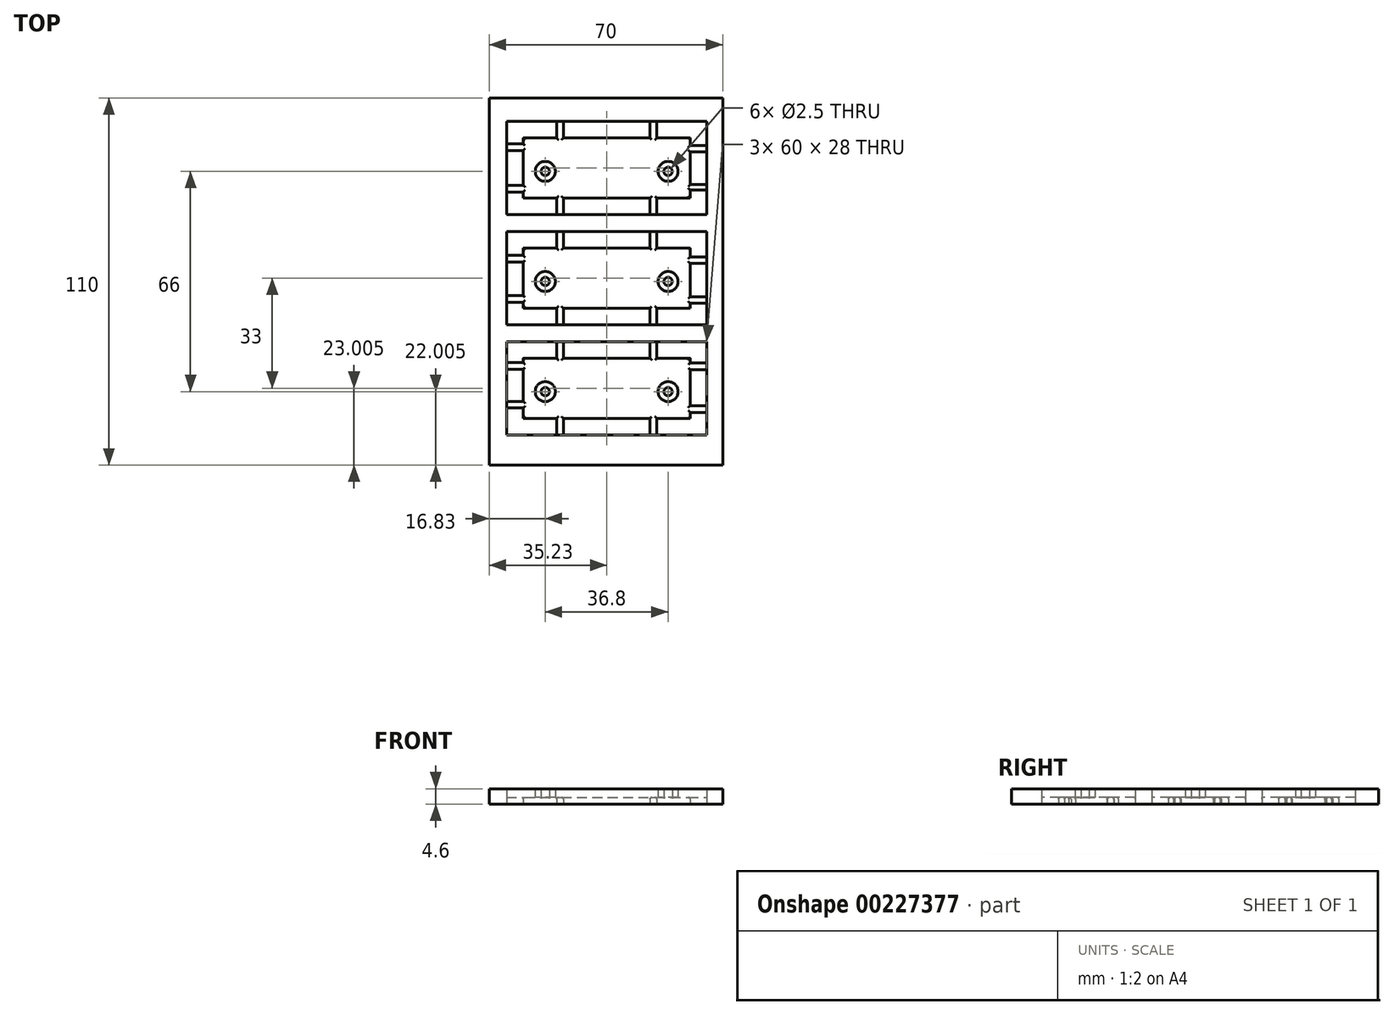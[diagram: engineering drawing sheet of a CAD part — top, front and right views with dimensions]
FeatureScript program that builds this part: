
annotation { "Feature Type Name" : "Feature", "Feature Type Description" : "" }
export const myFeature = defineFeature(function(context is Context, id is Id, definition is map)
    precondition{}
    {
        {
            var Q0;
            Q0=qCreatedBy(makeId("Top.planeOp"),FACE);
            var sketch = newSketch(context, id + "F0", { "sketchPlane" : qUnion([Q0])});
            skLineSegment(sketch, "E0.bottom", {"start": v(-14.26, 31.33) * mm, "end": v(35.74, 31.33) * mm});
            skLineSegment(sketch, "E0.top", {"start": v(-14.26, 13.33) * mm, "end": v(35.74, 13.33) * mm});
            skLineSegment(sketch, "E0.left", {"start": v(-14.26, 31.33) * mm, "end": v(-14.26, 13.33) * mm});
            skLineSegment(sketch, "E0.right", {"start": v(35.74, 31.33) * mm, "end": v(35.74, 13.33) * mm});
            skLineSegment(sketch, "E1.bottom", {"start": v(-14.26, -1.67) * mm, "end": v(35.74, -1.67) * mm});
            skLineSegment(sketch, "E1.top", {"start": v(-14.26, -19.67) * mm, "end": v(35.74, -19.67) * mm});
            skLineSegment(sketch, "E1.left", {"start": v(-14.26, -1.67) * mm, "end": v(-14.26, -19.67) * mm});
            skLineSegment(sketch, "E1.right", {"start": v(35.74, -1.67) * mm, "end": v(35.74, -19.67) * mm});
            skLineSegment(sketch, "E2.bottom", {"start": v(-14.26, -34.67) * mm, "end": v(35.74, -34.67) * mm});
            skLineSegment(sketch, "E2.top", {"start": v(-14.26, -52.67) * mm, "end": v(35.74, -52.67) * mm});
            skLineSegment(sketch, "E2.left", {"start": v(-14.26, -34.67) * mm, "end": v(-14.26, -52.67) * mm});
            skLineSegment(sketch, "E2.right", {"start": v(35.74, -34.67) * mm, "end": v(35.74, -52.67) * mm});
            skLineSegment(sketch, "E3.bottom", {"start": v(-4.26, 31.33) * mm, "end": v(-2.26, 31.33) * mm});
            skLineSegment(sketch, "E3.top", {"start": v(-4.26, 36.33) * mm, "end": v(-2.26, 36.33) * mm});
            skLineSegment(sketch, "E3.left", {"start": v(-4.26, 31.33) * mm, "end": v(-4.26, 36.33) * mm});
            skLineSegment(sketch, "E3.right", {"start": v(-2.26, 31.33) * mm, "end": v(-2.26, 36.33) * mm});
            skLineSegment(sketch, "E4.bottom", {"start": v(23.74, 36.33) * mm, "end": v(25.74, 36.33) * mm});
            skLineSegment(sketch, "E4.top", {"start": v(23.74, 31.33) * mm, "end": v(25.74, 31.33) * mm});
            skLineSegment(sketch, "E4.left", {"start": v(23.74, 36.33) * mm, "end": v(23.74, 31.33) * mm});
            skLineSegment(sketch, "E4.right", {"start": v(25.74, 36.33) * mm, "end": v(25.74, 31.33) * mm});
            skPoint(sketch, "E5.firstSnap0", {"position": v(-4.26, 33.83) * mm});
            skLineSegment(sketch, "E5.bottom", {"start": v(-4.26, 13.33) * mm, "end": v(-2.26, 13.33) * mm});
            skLineSegment(sketch, "E5.top", {"start": v(-4.26, 8.33) * mm, "end": v(-2.26, 8.33) * mm});
            skLineSegment(sketch, "E5.left", {"start": v(-4.26, 13.33) * mm, "end": v(-4.26, 8.33) * mm});
            skLineSegment(sketch, "E5.right", {"start": v(-2.26, 13.33) * mm, "end": v(-2.26, 8.33) * mm});
            skLineSegment(sketch, "E6.bottom", {"start": v(23.74, 13.33) * mm, "end": v(25.74, 13.33) * mm});
            skLineSegment(sketch, "E6.top", {"start": v(23.74, 8.33) * mm, "end": v(25.74, 8.33) * mm});
            skLineSegment(sketch, "E6.left", {"start": v(23.74, 13.33) * mm, "end": v(23.74, 8.33) * mm});
            skLineSegment(sketch, "E6.right", {"start": v(25.74, 13.33) * mm, "end": v(25.74, 8.33) * mm});
            skLineSegment(sketch, "E7.bottom", {"start": v(-4.26, -1.67) * mm, "end": v(-2.26, -1.67) * mm});
            skLineSegment(sketch, "E7.top", {"start": v(-4.26, 3.33) * mm, "end": v(-2.26, 3.33) * mm});
            skLineSegment(sketch, "E7.left", {"start": v(-4.26, -1.67) * mm, "end": v(-4.26, 3.33) * mm});
            skLineSegment(sketch, "E7.right", {"start": v(-2.26, -1.67) * mm, "end": v(-2.26, 3.33) * mm});
            skLineSegment(sketch, "E8.bottom", {"start": v(23.74, 3.33) * mm, "end": v(25.74, 3.33) * mm});
            skLineSegment(sketch, "E8.top", {"start": v(23.74, -1.67) * mm, "end": v(25.74, -1.67) * mm});
            skLineSegment(sketch, "E8.left", {"start": v(23.74, 3.33) * mm, "end": v(23.74, -1.67) * mm});
            skLineSegment(sketch, "E8.right", {"start": v(25.74, 3.33) * mm, "end": v(25.74, -1.67) * mm});
            skLineSegment(sketch, "E9.bottom", {"start": v(-4.26, -19.67) * mm, "end": v(-2.26, -19.67) * mm});
            skLineSegment(sketch, "E9.top", {"start": v(-4.26, -24.67) * mm, "end": v(-2.26, -24.67) * mm});
            skLineSegment(sketch, "E9.left", {"start": v(-4.26, -19.67) * mm, "end": v(-4.26, -24.67) * mm});
            skLineSegment(sketch, "E9.right", {"start": v(-2.26, -19.67) * mm, "end": v(-2.26, -24.67) * mm});
            skLineSegment(sketch, "E10.bottom", {"start": v(23.74, -19.67) * mm, "end": v(25.74, -19.67) * mm});
            skLineSegment(sketch, "E10.top", {"start": v(23.74, -24.67) * mm, "end": v(25.74, -24.67) * mm});
            skLineSegment(sketch, "E10.left", {"start": v(23.74, -19.67) * mm, "end": v(23.74, -24.67) * mm});
            skLineSegment(sketch, "E10.right", {"start": v(25.74, -19.67) * mm, "end": v(25.74, -24.67) * mm});
            skLineSegment(sketch, "E11.bottom", {"start": v(-4.26, -29.67) * mm, "end": v(-2.26, -29.67) * mm});
            skLineSegment(sketch, "E11.top", {"start": v(-4.26, -34.67) * mm, "end": v(-2.26, -34.67) * mm});
            skLineSegment(sketch, "E11.left", {"start": v(-4.26, -29.67) * mm, "end": v(-4.26, -34.67) * mm});
            skLineSegment(sketch, "E11.right", {"start": v(-2.26, -29.67) * mm, "end": v(-2.26, -34.67) * mm});
            skLineSegment(sketch, "E12.bottom", {"start": v(23.74, -29.67) * mm, "end": v(25.74, -29.67) * mm});
            skLineSegment(sketch, "E12.top", {"start": v(23.74, -34.67) * mm, "end": v(25.74, -34.67) * mm});
            skLineSegment(sketch, "E12.left", {"start": v(23.74, -29.67) * mm, "end": v(23.74, -34.67) * mm});
            skLineSegment(sketch, "E12.right", {"start": v(25.74, -29.67) * mm, "end": v(25.74, -34.67) * mm});
            skLineSegment(sketch, "E13.bottom", {"start": v(-4.26, -52.67) * mm, "end": v(-2.26, -52.67) * mm});
            skLineSegment(sketch, "E13.top", {"start": v(-4.26, -57.67) * mm, "end": v(-2.26, -57.67) * mm});
            skLineSegment(sketch, "E13.left", {"start": v(-4.26, -52.67) * mm, "end": v(-4.26, -57.67) * mm});
            skLineSegment(sketch, "E13.right", {"start": v(-2.26, -52.67) * mm, "end": v(-2.26, -57.67) * mm});
            skLineSegment(sketch, "E14.bottom", {"start": v(23.74, -52.67) * mm, "end": v(25.74, -52.67) * mm});
            skLineSegment(sketch, "E14.top", {"start": v(23.74, -57.67) * mm, "end": v(25.74, -57.67) * mm});
            skLineSegment(sketch, "E14.left", {"start": v(23.74, -52.67) * mm, "end": v(23.74, -57.67) * mm});
            skLineSegment(sketch, "E14.right", {"start": v(25.74, -52.67) * mm, "end": v(25.74, -57.67) * mm});
            skLineSegment(sketch, "E15.left", {"start": v(-14.26, 22.33) * mm, "end": v(-14.26, 20.33) * mm});
            skLineSegment(sketch, "E16.left", {"start": v(35.74, 22.33) * mm, "end": v(35.74, 20.33) * mm});
            skLineSegment(sketch, "E17.left", {"start": v(35.74, -10.67) * mm, "end": v(35.74, -12.67) * mm});
            skLineSegment(sketch, "E18.left", {"start": v(-14.26, -10.67) * mm, "end": v(-14.26, -12.67) * mm});
            skLineSegment(sketch, "E19.left", {"start": v(35.74, -43.67) * mm, "end": v(35.74, -45.67) * mm});
            skPoint(sketch, "E20.oppositeSnap0", {"position": v(-14.26, -43.67) * mm});
            skLineSegment(sketch, "E20.left", {"start": v(-14.26, -41.67) * mm, "end": v(-14.26, -43.67) * mm});
            skCircle(sketch, "E21", {"center": v(-7.66, 21.33) * mm, "radius": 3 * mm});
            skCircle(sketch, "E22", {"center": v(-7.66, 21.33) * mm, "radius": 1.25 * mm});
            skCircle(sketch, "E23", {"center": v(29.14, 21.33) * mm, "radius": 3 * mm});
            skCircle(sketch, "E24", {"center": v(29.14, 21.33) * mm, "radius": 1.25 * mm});
            skCircle(sketch, "E25", {"center": v(-7.66, -11.67) * mm, "radius": 3 * mm});
            skCircle(sketch, "E26", {"center": v(-7.66, -11.67) * mm, "radius": 1.25 * mm});
            skCircle(sketch, "E27", {"center": v(29.14, -11.67) * mm, "radius": 3 * mm});
            skCircle(sketch, "E28", {"center": v(29.14, -11.67) * mm, "radius": 1.25 * mm});
            skCircle(sketch, "E29", {"center": v(-7.66, -44.67) * mm, "radius": 3 * mm});
            skCircle(sketch, "E30", {"center": v(-7.66, -44.67) * mm, "radius": 1.25 * mm});
            skCircle(sketch, "E31", {"center": v(29.14, -44.67) * mm, "radius": 3 * mm});
            skCircle(sketch, "E32", {"center": v(29.14, -44.67) * mm, "radius": 1.25 * mm});
            skLineSegment(sketch, "E33.top", {"start": v(8.74, 31.33) * mm, "end": v(10.74, 31.33) * mm});
            skLineSegment(sketch, "E34.bottom", {"start": v(8.74, 13.33) * mm, "end": v(10.74, 13.33) * mm});
            skLineSegment(sketch, "E35.top", {"start": v(8.74, -1.67) * mm, "end": v(10.74, -1.67) * mm});
            skLineSegment(sketch, "E36.bottom", {"start": v(8.78, -19.67) * mm, "end": v(10.78, -19.67) * mm});
            skLineSegment(sketch, "E37.top", {"start": v(8.74, -34.67) * mm, "end": v(10.74, -34.67) * mm});
            skLineSegment(sketch, "E38.bottom", {"start": v(8.3, -52.67) * mm, "end": v(10.3, -52.67) * mm});
            skLineSegment(sketch, "E39.bottom", {"start": v(-19.26, -15.88) * mm, "end": v(-14.26, -15.88) * mm});
            skLineSegment(sketch, "E39.top", {"start": v(-19.26, -17.87) * mm, "end": v(-14.26, -17.87) * mm});
            skLineSegment(sketch, "E39.left", {"start": v(-19.26, -15.88) * mm, "end": v(-19.26, -17.87) * mm});
            skLineSegment(sketch, "E39.right", {"start": v(-14.26, -15.88) * mm, "end": v(-14.26, -17.87) * mm});
            skLineSegment(sketch, "E40.bottom", {"start": v(-19.26, -3.86) * mm, "end": v(-14.26, -3.86) * mm});
            skLineSegment(sketch, "E40.top", {"start": v(-19.26, -5.86) * mm, "end": v(-14.26, -5.86) * mm});
            skLineSegment(sketch, "E40.left", {"start": v(-19.26, -3.86) * mm, "end": v(-19.26, -5.86) * mm});
            skLineSegment(sketch, "E40.right", {"start": v(-14.26, -3.86) * mm, "end": v(-14.26, -5.86) * mm});
            skLineSegment(sketch, "E41.bottom", {"start": v(35.74, -4.26) * mm, "end": v(40.74, -4.26) * mm});
            skLineSegment(sketch, "E41.top", {"start": v(35.74, -6.26) * mm, "end": v(40.74, -6.26) * mm});
            skLineSegment(sketch, "E41.left", {"start": v(35.74, -4.26) * mm, "end": v(35.74, -6.26) * mm});
            skLineSegment(sketch, "E41.right", {"start": v(40.74, -4.26) * mm, "end": v(40.74, -6.26) * mm});
            skLineSegment(sketch, "E42.bottom", {"start": v(35.74, -16.2) * mm, "end": v(40.74, -16.2) * mm});
            skLineSegment(sketch, "E42.top", {"start": v(35.74, -18.2) * mm, "end": v(40.74, -18.2) * mm});
            skLineSegment(sketch, "E42.left", {"start": v(35.74, -16.2) * mm, "end": v(35.74, -18.2) * mm});
            skLineSegment(sketch, "E42.right", {"start": v(40.74, -16.2) * mm, "end": v(40.74, -18.2) * mm});
            skLineSegment(sketch, "E43.bottom", {"start": v(35.74, 29.13) * mm, "end": v(40.74, 29.13) * mm});
            skLineSegment(sketch, "E43.top", {"start": v(35.74, 27.12) * mm, "end": v(40.74, 27.12) * mm});
            skLineSegment(sketch, "E43.left", {"start": v(35.74, 29.13) * mm, "end": v(35.74, 27.12) * mm});
            skLineSegment(sketch, "E43.right", {"start": v(40.74, 29.13) * mm, "end": v(40.74, 27.12) * mm});
            skLineSegment(sketch, "E44.bottom", {"start": v(35.74, 17.34) * mm, "end": v(40.74, 17.34) * mm});
            skLineSegment(sketch, "E44.top", {"start": v(35.74, 15.76) * mm, "end": v(40.74, 15.76) * mm});
            skLineSegment(sketch, "E44.left", {"start": v(35.74, 17.34) * mm, "end": v(35.74, 15.76) * mm});
            skLineSegment(sketch, "E44.right", {"start": v(40.74, 17.34) * mm, "end": v(40.74, 15.76) * mm});
            skLineSegment(sketch, "E45.bottom", {"start": v(-19.26, -47.57) * mm, "end": v(-14.26, -47.57) * mm});
            skLineSegment(sketch, "E45.top", {"start": v(-19.26, -49.57) * mm, "end": v(-14.26, -49.57) * mm});
            skLineSegment(sketch, "E45.left", {"start": v(-19.26, -47.57) * mm, "end": v(-19.26, -49.57) * mm});
            skLineSegment(sketch, "E45.right", {"start": v(-14.26, -47.57) * mm, "end": v(-14.26, -49.57) * mm});
            skLineSegment(sketch, "E46.bottom", {"start": v(-19.26, 29.6) * mm, "end": v(-14.26, 29.6) * mm});
            skLineSegment(sketch, "E46.top", {"start": v(-19.26, 27.6) * mm, "end": v(-14.26, 27.6) * mm});
            skLineSegment(sketch, "E46.left", {"start": v(-19.26, 29.6) * mm, "end": v(-19.26, 27.6) * mm});
            skLineSegment(sketch, "E46.right", {"start": v(-14.26, 29.6) * mm, "end": v(-14.26, 27.6) * mm});
            skLineSegment(sketch, "E47.bottom", {"start": v(-19.26, 17.17) * mm, "end": v(-14.26, 17.17) * mm});
            skLineSegment(sketch, "E47.top", {"start": v(-19.26, 15.17) * mm, "end": v(-14.26, 15.17) * mm});
            skLineSegment(sketch, "E47.left", {"start": v(-19.26, 17.17) * mm, "end": v(-19.26, 15.17) * mm});
            skLineSegment(sketch, "E47.right", {"start": v(-14.26, 17.17) * mm, "end": v(-14.26, 15.17) * mm});
            skLineSegment(sketch, "E48.bottom", {"start": v(35.74, -36.08) * mm, "end": v(40.74, -36.08) * mm});
            skLineSegment(sketch, "E48.top", {"start": v(35.74, -38.08) * mm, "end": v(40.74, -38.08) * mm});
            skLineSegment(sketch, "E48.left", {"start": v(35.74, -36.08) * mm, "end": v(35.74, -38.08) * mm});
            skLineSegment(sketch, "E48.right", {"start": v(40.74, -36.08) * mm, "end": v(40.74, -38.08) * mm});
            skLineSegment(sketch, "E49.bottom", {"start": v(35.74, -48.86) * mm, "end": v(40.74, -48.86) * mm});
            skLineSegment(sketch, "E49.top", {"start": v(35.74, -50.86) * mm, "end": v(40.74, -50.86) * mm});
            skLineSegment(sketch, "E49.left", {"start": v(35.74, -48.86) * mm, "end": v(35.74, -50.86) * mm});
            skLineSegment(sketch, "E49.right", {"start": v(40.74, -48.86) * mm, "end": v(40.74, -50.86) * mm});
            skLineSegment(sketch, "E50.bottom", {"start": v(-19.26, -35.96) * mm, "end": v(-14.26, -35.96) * mm});
            skLineSegment(sketch, "E50.top", {"start": v(-19.26, -37.96) * mm, "end": v(-14.26, -37.96) * mm});
            skLineSegment(sketch, "E50.left", {"start": v(-19.26, -35.96) * mm, "end": v(-19.26, -37.96) * mm});
            skLineSegment(sketch, "E50.right", {"start": v(-14.26, -35.96) * mm, "end": v(-14.26, -37.96) * mm});
            skSolve(sketch);
        }
        {
            var Q0;
            Q0=qSketchRegion(id+"F0",true);
            extrude(context, id + "F1", {"entities" : qUnion([Q0]), "depth" : 2 * mm});
        }
        {
            var Q0;
            Q0=qCreatedBy(makeId("Top.planeOp"),FACE);
            var sketch = newSketch(context, id + "F2", { "sketchPlane" : qUnion([Q0])});
            skLineSegment(sketch, "E51.bottom", {"start": v(-19.26, 36.33) * mm, "end": v(40.74, 36.33) * mm});
            skLineSegment(sketch, "E51.top", {"start": v(-19.26, 8.33) * mm, "end": v(40.74, 8.33) * mm});
            skLineSegment(sketch, "E51.left", {"start": v(-19.26, 36.33) * mm, "end": v(-19.26, 8.33) * mm});
            skLineSegment(sketch, "E51.right", {"start": v(40.74, 36.33) * mm, "end": v(40.74, 8.33) * mm});
            skLineSegment(sketch, "E52.bottom", {"start": v(-19.26, 3.33) * mm, "end": v(40.74, 3.33) * mm});
            skLineSegment(sketch, "E52.top", {"start": v(-19.26, -24.67) * mm, "end": v(40.74, -24.67) * mm});
            skLineSegment(sketch, "E52.left", {"start": v(-19.26, 3.33) * mm, "end": v(-19.26, -24.67) * mm});
            skLineSegment(sketch, "E52.right", {"start": v(40.74, 3.33) * mm, "end": v(40.74, -24.67) * mm});
            skLineSegment(sketch, "E53.bottom", {"start": v(-19.26, -29.67) * mm, "end": v(40.74, -29.67) * mm});
            skLineSegment(sketch, "E53.top", {"start": v(-19.26, -57.67) * mm, "end": v(40.74, -57.67) * mm});
            skLineSegment(sketch, "E53.left", {"start": v(-19.26, -29.67) * mm, "end": v(-19.26, -57.67) * mm});
            skLineSegment(sketch, "E53.right", {"start": v(40.74, -29.67) * mm, "end": v(40.74, -57.67) * mm});
            skLineSegment(sketch, "E54.bottom", {"start": v(-24.5, 43.33) * mm, "end": v(45.5, 43.33) * mm});
            skLineSegment(sketch, "E54.top", {"start": v(-24.5, -66.67) * mm, "end": v(45.5, -66.67) * mm});
            skLineSegment(sketch, "E54.left", {"start": v(-24.5, 43.33) * mm, "end": v(-24.5, -66.67) * mm});
            skLineSegment(sketch, "E54.right", {"start": v(45.5, 43.33) * mm, "end": v(45.5, -66.67) * mm});
            skSolve(sketch);
        }
        {
            var Q0;
            Q0=qSketchRegion(id+"F2",true);
            extrude(context, id + "F3", {"entities" : qUnion([Q0]), "depth" : 4.6 * mm});
        }
        {
            var Q0;
            Q0=makeQuery(id+"F0.imprint","IMPRINT",FACE,{"disambiguationData":[TD([[makeQuery(id+"F0.imprint","IMPRINT",EDGE,{"derivedFrom":sQuery(id+"F0.wireOp",EDGE,"E21")}),1.0]])]});
            var Q1;
            Q1=makeQuery(id+"F0.imprint","IMPRINT",FACE,{"disambiguationData":[TD([[makeQuery(id+"F0.imprint","IMPRINT",EDGE,{"derivedFrom":sQuery(id+"F0.wireOp",EDGE,"E23")}),1.0]])]});
            var Q2;
            Q2=makeQuery(id+"F0.imprint","IMPRINT",FACE,{"disambiguationData":[TD([[makeQuery(id+"F0.imprint","IMPRINT",EDGE,{"derivedFrom":sQuery(id+"F0.wireOp",EDGE,"E25")}),1.0]])]});
            var Q3;
            Q3=makeQuery(id+"F0.imprint","IMPRINT",FACE,{"disambiguationData":[TD([[makeQuery(id+"F0.imprint","IMPRINT",EDGE,{"derivedFrom":sQuery(id+"F0.wireOp",EDGE,"E27")}),1.0]])]});
            var Q4;
            Q4=makeQuery(id+"F0.imprint","IMPRINT",FACE,{"disambiguationData":[TD([[makeQuery(id+"F0.imprint","IMPRINT",EDGE,{"derivedFrom":sQuery(id+"F0.wireOp",EDGE,"E29")}),1.0]])]});
            var Q5;
            Q5=makeQuery(id+"F0.imprint","IMPRINT",FACE,{"disambiguationData":[TD([[makeQuery(id+"F0.imprint","IMPRINT",EDGE,{"derivedFrom":sQuery(id+"F0.wireOp",EDGE,"E31")}),1.0]])]});
            extrude(context, id + "F4", {"entities" : qUnion([Q0, Q1, Q2, Q3, Q4, Q5]), "operationType" : NewBodyOperationType.ADD, "depth" : 4.6 * mm});
        }
        {
            var Q0;
            Q0=makeQuery(id+"F1.opExtrude","CAP_EDGE",EDGE,{"disambiguationData":[OSD([sQuery(id+"F0.wireOp",EDGE,"E5.right")])],"isStart":false});
            var Q1;
            Q1=makeQuery(id+"F1.opExtrude","CAP_EDGE",EDGE,{"disambiguationData":[OSD([sQuery(id+"F0.wireOp",EDGE,"E0.top"),sQuery(id+"F0.wireOp",EDGE,"E34.bottom")])],"isStart":false});
            var Q2;
            Q2=makeQuery(id+"F1.opExtrude","CAP_EDGE",EDGE,{"disambiguationData":[OSD([sQuery(id+"F0.wireOp",EDGE,"E5.left")])],"isStart":false});
            var Q3;
            {var subQ0=sQuery(id+"F0.wireOp",EDGE,"E0.top");Q3=makeQuery(id+"F1.opExtrude","CAP_EDGE",EDGE,{"disambiguationData":[OSD([subQ0]),TDD([makeQuery(id+"F0.imprint","IMPRINT",EDGE,{"disambiguationData":[TD([[makeQuery(id+"F0.imprint","INTERSECT",VERTEX,{"derivedFrom":[subQ0,sQuery(id+"F0.wireOp",EDGE,"E0.left")]}),-1.0]])],"derivedFrom":subQ0})])],"isStart":false});}
            var Q4;
            {var subQ0=sQuery(id+"F0.wireOp",EDGE,"E0.left");Q4=makeQuery(id+"F1.opExtrude","CAP_EDGE",EDGE,{"disambiguationData":[OSD([subQ0]),TDD([makeQuery(id+"F0.imprint","IMPRINT",EDGE,{"disambiguationData":[TD([[makeQuery(id+"F0.imprint","INTERSECT",VERTEX,{"derivedFrom":[sQuery(id+"F0.wireOp",EDGE,"E0.top"),subQ0]}),1.0]])],"derivedFrom":subQ0})])],"isStart":false});}
            var Q5;
            Q5=makeQuery(id+"F1.opExtrude","CAP_EDGE",EDGE,{"disambiguationData":[OSD([sQuery(id+"F0.wireOp",EDGE,"E47.top")])],"isStart":false});
            var Q6;
            Q6=makeQuery(id+"F1.opExtrude","CAP_EDGE",EDGE,{"disambiguationData":[OSD([sQuery(id+"F0.wireOp",EDGE,"E47.bottom")])],"isStart":false});
            var Q7;
            Q7=makeQuery(id+"F1.opExtrude","CAP_EDGE",EDGE,{"disambiguationData":[OSD([sQuery(id+"F0.wireOp",EDGE,"E0.left"),sQuery(id+"F0.wireOp",EDGE,"E15.left")])],"isStart":false});
            var Q8;
            Q8=makeQuery(id+"F1.opExtrude","CAP_EDGE",EDGE,{"disambiguationData":[OSD([sQuery(id+"F0.wireOp",EDGE,"E46.top")])],"isStart":false});
            var Q9;
            Q9=makeQuery(id+"F1.opExtrude","CAP_EDGE",EDGE,{"disambiguationData":[OSD([sQuery(id+"F0.wireOp",EDGE,"E46.bottom")])],"isStart":false});
            var Q10;
            {var subQ0=sQuery(id+"F0.wireOp",EDGE,"E0.bottom");Q10=makeQuery(id+"F1.opExtrude","CAP_EDGE",EDGE,{"disambiguationData":[OSD([subQ0]),TDD([makeQuery(id+"F0.imprint","IMPRINT",EDGE,{"disambiguationData":[TD([[makeQuery(id+"F0.imprint","INTERSECT",VERTEX,{"derivedFrom":[subQ0,sQuery(id+"F0.wireOp",EDGE,"E0.left")]}),-1.0]])],"derivedFrom":subQ0})])],"isStart":false});}
            var Q11;
            {var subQ0=sQuery(id+"F0.wireOp",EDGE,"E0.left");Q11=makeQuery(id+"F1.opExtrude","CAP_EDGE",EDGE,{"disambiguationData":[OSD([subQ0]),TDD([makeQuery(id+"F0.imprint","IMPRINT",EDGE,{"disambiguationData":[TD([[makeQuery(id+"F0.imprint","INTERSECT",VERTEX,{"derivedFrom":[sQuery(id+"F0.wireOp",EDGE,"E0.bottom"),subQ0]}),-1.0]])],"derivedFrom":subQ0})])],"isStart":false});}
            var Q12;
            Q12=makeQuery(id+"F1.opExtrude","CAP_EDGE",EDGE,{"disambiguationData":[OSD([sQuery(id+"F0.wireOp",EDGE,"E3.left")])],"isStart":false});
            var Q13;
            Q13=makeQuery(id+"F1.opExtrude","CAP_EDGE",EDGE,{"disambiguationData":[OSD([sQuery(id+"F0.wireOp",EDGE,"E3.right")])],"isStart":false});
            var Q14;
            Q14=makeQuery(id+"F1.opExtrude","CAP_EDGE",EDGE,{"disambiguationData":[OSD([sQuery(id+"F0.wireOp",EDGE,"E0.bottom"),sQuery(id+"F0.wireOp",EDGE,"E33.top")])],"isStart":false});
            var Q15;
            Q15=makeQuery(id+"F1.opExtrude","CAP_EDGE",EDGE,{"disambiguationData":[OSD([sQuery(id+"F0.wireOp",EDGE,"E4.left")])],"isStart":false});
            var Q16;
            Q16=makeQuery(id+"F1.opExtrude","CAP_EDGE",EDGE,{"disambiguationData":[OSD([sQuery(id+"F0.wireOp",EDGE,"E4.right")])],"isStart":false});
            var Q17;
            {var subQ0=sQuery(id+"F0.wireOp",EDGE,"E0.bottom");Q17=makeQuery(id+"F1.opExtrude","CAP_EDGE",EDGE,{"disambiguationData":[OSD([subQ0]),TDD([makeQuery(id+"F0.imprint","IMPRINT",EDGE,{"disambiguationData":[TD([[makeQuery(id+"F0.imprint","INTERSECT",VERTEX,{"derivedFrom":[subQ0,sQuery(id+"F0.wireOp",EDGE,"E0.right")]}),1.0]])],"derivedFrom":subQ0})])],"isStart":false});}
            var Q18;
            {var subQ0=sQuery(id+"F0.wireOp",EDGE,"E0.right");Q18=makeQuery(id+"F1.opExtrude","CAP_EDGE",EDGE,{"disambiguationData":[OSD([subQ0]),TDD([makeQuery(id+"F0.imprint","IMPRINT",EDGE,{"disambiguationData":[TD([[makeQuery(id+"F0.imprint","INTERSECT",VERTEX,{"derivedFrom":[sQuery(id+"F0.wireOp",EDGE,"E0.bottom"),subQ0]}),-1.0]])],"derivedFrom":subQ0})])],"isStart":false});}
            var Q19;
            Q19=makeQuery(id+"F1.opExtrude","CAP_EDGE",EDGE,{"disambiguationData":[OSD([sQuery(id+"F0.wireOp",EDGE,"E43.bottom")])],"isStart":false});
            var Q20;
            Q20=makeQuery(id+"F1.opExtrude","CAP_EDGE",EDGE,{"disambiguationData":[OSD([sQuery(id+"F0.wireOp",EDGE,"E43.top")])],"isStart":false});
            var Q21;
            Q21=makeQuery(id+"F1.opExtrude","CAP_EDGE",EDGE,{"disambiguationData":[OSD([sQuery(id+"F0.wireOp",EDGE,"E0.right"),sQuery(id+"F0.wireOp",EDGE,"E16.left")])],"isStart":false});
            var Q22;
            Q22=makeQuery(id+"F1.opExtrude","CAP_EDGE",EDGE,{"disambiguationData":[OSD([sQuery(id+"F0.wireOp",EDGE,"E44.bottom")])],"isStart":false});
            var Q23;
            Q23=makeQuery(id+"F1.opExtrude","CAP_EDGE",EDGE,{"disambiguationData":[OSD([sQuery(id+"F0.wireOp",EDGE,"E44.top")])],"isStart":false});
            var Q24;
            {var subQ0=sQuery(id+"F0.wireOp",EDGE,"E0.right");Q24=makeQuery(id+"F1.opExtrude","CAP_EDGE",EDGE,{"disambiguationData":[OSD([subQ0]),TDD([makeQuery(id+"F0.imprint","IMPRINT",EDGE,{"disambiguationData":[TD([[makeQuery(id+"F0.imprint","INTERSECT",VERTEX,{"derivedFrom":[sQuery(id+"F0.wireOp",EDGE,"E0.top"),subQ0]}),1.0]])],"derivedFrom":subQ0})])],"isStart":false});}
            var Q25;
            {var subQ0=sQuery(id+"F0.wireOp",EDGE,"E0.top");Q25=makeQuery(id+"F1.opExtrude","CAP_EDGE",EDGE,{"disambiguationData":[OSD([subQ0]),TDD([makeQuery(id+"F0.imprint","IMPRINT",EDGE,{"disambiguationData":[TD([[makeQuery(id+"F0.imprint","INTERSECT",VERTEX,{"derivedFrom":[subQ0,sQuery(id+"F0.wireOp",EDGE,"E0.right")]}),1.0]])],"derivedFrom":subQ0})])],"isStart":false});}
            var Q26;
            Q26=makeQuery(id+"F1.opExtrude","CAP_EDGE",EDGE,{"disambiguationData":[OSD([sQuery(id+"F0.wireOp",EDGE,"E6.right")])],"isStart":false});
            var Q27;
            Q27=makeQuery(id+"F1.opExtrude","CAP_EDGE",EDGE,{"disambiguationData":[OSD([sQuery(id+"F0.wireOp",EDGE,"E6.left")])],"isStart":false});
            fillet(context, id + "F5", {"entities" : qUnion([Q0, Q1, Q2, Q3, Q4, Q5, Q6, Q7, Q8, Q9, Q10, Q11, Q12, Q13, Q14, Q15, Q16, Q17, Q18, Q19, Q20, Q21, Q22, Q23, Q24, Q25, Q26, Q27]), "radius" : 0.5 * mm, "tangentPropagation" : true, "allowEdgeOverflow" : false});
        }
        {
            var Q0;
            Q0=makeQuery(id+"F1.opExtrude","CAP_EDGE",EDGE,{"disambiguationData":[OSD([sQuery(id+"F0.wireOp",EDGE,"E1.bottom"),sQuery(id+"F0.wireOp",EDGE,"E35.top")])],"isStart":false});
            var Q1;
            Q1=makeQuery(id+"F1.opExtrude","CAP_EDGE",EDGE,{"disambiguationData":[OSD([sQuery(id+"F0.wireOp",EDGE,"E7.right")])],"isStart":false});
            var Q2;
            Q2=makeQuery(id+"F1.opExtrude","CAP_EDGE",EDGE,{"disambiguationData":[OSD([sQuery(id+"F0.wireOp",EDGE,"E7.left")])],"isStart":false});
            var Q3;
            {var subQ0=sQuery(id+"F0.wireOp",EDGE,"E1.bottom");Q3=makeQuery(id+"F1.opExtrude","CAP_EDGE",EDGE,{"disambiguationData":[OSD([subQ0]),TDD([makeQuery(id+"F0.imprint","IMPRINT",EDGE,{"disambiguationData":[TD([[makeQuery(id+"F0.imprint","INTERSECT",VERTEX,{"derivedFrom":[subQ0,sQuery(id+"F0.wireOp",EDGE,"E1.left")]}),-1.0]])],"derivedFrom":subQ0})])],"isStart":false});}
            var Q4;
            {var subQ0=sQuery(id+"F0.wireOp",EDGE,"E1.left");Q4=makeQuery(id+"F1.opExtrude","CAP_EDGE",EDGE,{"disambiguationData":[OSD([subQ0]),TDD([makeQuery(id+"F0.imprint","IMPRINT",EDGE,{"disambiguationData":[TD([[makeQuery(id+"F0.imprint","INTERSECT",VERTEX,{"derivedFrom":[sQuery(id+"F0.wireOp",EDGE,"E1.bottom"),subQ0]}),-1.0]])],"derivedFrom":subQ0})])],"isStart":false});}
            var Q5;
            Q5=makeQuery(id+"F1.opExtrude","CAP_EDGE",EDGE,{"disambiguationData":[OSD([sQuery(id+"F0.wireOp",EDGE,"E40.bottom")])],"isStart":false});
            var Q6;
            Q6=makeQuery(id+"F1.opExtrude","CAP_EDGE",EDGE,{"disambiguationData":[OSD([sQuery(id+"F0.wireOp",EDGE,"E40.top")])],"isStart":false});
            var Q7;
            Q7=makeQuery(id+"F1.opExtrude","CAP_EDGE",EDGE,{"disambiguationData":[OSD([sQuery(id+"F0.wireOp",EDGE,"E1.left"),sQuery(id+"F0.wireOp",EDGE,"E18.left")])],"isStart":false});
            var Q8;
            Q8=makeQuery(id+"F1.opExtrude","CAP_EDGE",EDGE,{"disambiguationData":[OSD([sQuery(id+"F0.wireOp",EDGE,"E39.bottom")])],"isStart":false});
            var Q9;
            Q9=makeQuery(id+"F1.opExtrude","CAP_EDGE",EDGE,{"disambiguationData":[OSD([sQuery(id+"F0.wireOp",EDGE,"E39.top")])],"isStart":false});
            var Q10;
            {var subQ0=sQuery(id+"F0.wireOp",EDGE,"E1.left");Q10=makeQuery(id+"F1.opExtrude","CAP_EDGE",EDGE,{"disambiguationData":[OSD([subQ0]),TDD([makeQuery(id+"F0.imprint","IMPRINT",EDGE,{"disambiguationData":[TD([[makeQuery(id+"F0.imprint","INTERSECT",VERTEX,{"derivedFrom":[sQuery(id+"F0.wireOp",EDGE,"E1.top"),subQ0]}),1.0]])],"derivedFrom":subQ0})])],"isStart":false});}
            var Q11;
            {var subQ0=sQuery(id+"F0.wireOp",EDGE,"E1.top");Q11=makeQuery(id+"F1.opExtrude","CAP_EDGE",EDGE,{"disambiguationData":[OSD([subQ0]),TDD([makeQuery(id+"F0.imprint","IMPRINT",EDGE,{"disambiguationData":[TD([[makeQuery(id+"F0.imprint","INTERSECT",VERTEX,{"derivedFrom":[subQ0,sQuery(id+"F0.wireOp",EDGE,"E1.left")]}),-1.0]])],"derivedFrom":subQ0})])],"isStart":false});}
            var Q12;
            Q12=makeQuery(id+"F1.opExtrude","CAP_EDGE",EDGE,{"disambiguationData":[OSD([sQuery(id+"F0.wireOp",EDGE,"E9.left")])],"isStart":false});
            var Q13;
            Q13=makeQuery(id+"F1.opExtrude","CAP_EDGE",EDGE,{"disambiguationData":[OSD([sQuery(id+"F0.wireOp",EDGE,"E9.right")])],"isStart":false});
            var Q14;
            Q14=makeQuery(id+"F1.opExtrude","CAP_EDGE",EDGE,{"disambiguationData":[OSD([sQuery(id+"F0.wireOp",EDGE,"E1.top"),sQuery(id+"F0.wireOp",EDGE,"E36.bottom")])],"isStart":false});
            var Q15;
            Q15=makeQuery(id+"F1.opExtrude","CAP_EDGE",EDGE,{"disambiguationData":[OSD([sQuery(id+"F0.wireOp",EDGE,"E10.left")])],"isStart":false});
            var Q16;
            Q16=makeQuery(id+"F1.opExtrude","CAP_EDGE",EDGE,{"disambiguationData":[OSD([sQuery(id+"F0.wireOp",EDGE,"E10.right")])],"isStart":false});
            var Q17;
            {var subQ0=sQuery(id+"F0.wireOp",EDGE,"E1.top");Q17=makeQuery(id+"F1.opExtrude","CAP_EDGE",EDGE,{"disambiguationData":[OSD([subQ0]),TDD([makeQuery(id+"F0.imprint","IMPRINT",EDGE,{"disambiguationData":[TD([[makeQuery(id+"F0.imprint","INTERSECT",VERTEX,{"derivedFrom":[subQ0,sQuery(id+"F0.wireOp",EDGE,"E1.right")]}),1.0]])],"derivedFrom":subQ0})])],"isStart":false});}
            var Q18;
            Q18=makeQuery(id+"F1.opExtrude","CAP_EDGE",EDGE,{"disambiguationData":[OSD([sQuery(id+"F0.wireOp",EDGE,"E8.left")])],"isStart":false});
            var Q19;
            Q19=makeQuery(id+"F1.opExtrude","CAP_EDGE",EDGE,{"disambiguationData":[OSD([sQuery(id+"F0.wireOp",EDGE,"E8.right")])],"isStart":false});
            var Q20;
            {var subQ0=sQuery(id+"F0.wireOp",EDGE,"E1.bottom");Q20=makeQuery(id+"F1.opExtrude","CAP_EDGE",EDGE,{"disambiguationData":[OSD([subQ0]),TDD([makeQuery(id+"F0.imprint","IMPRINT",EDGE,{"disambiguationData":[TD([[makeQuery(id+"F0.imprint","INTERSECT",VERTEX,{"derivedFrom":[subQ0,sQuery(id+"F0.wireOp",EDGE,"E1.right")]}),1.0]])],"derivedFrom":subQ0})])],"isStart":false});}
            var Q21;
            Q21=makeQuery(id+"F1.opExtrude","CAP_EDGE",EDGE,{"disambiguationData":[OSD([sQuery(id+"F0.wireOp",EDGE,"E41.bottom")])],"isStart":false});
            var Q22;
            Q22=makeQuery(id+"F1.opExtrude","CAP_EDGE",EDGE,{"disambiguationData":[OSD([sQuery(id+"F0.wireOp",EDGE,"E1.right"),sQuery(id+"F0.wireOp",EDGE,"E17.left")])],"isStart":false});
            var Q23;
            {var subQ0=sQuery(id+"F0.wireOp",EDGE,"E1.right");Q23=makeQuery(id+"F1.opExtrude","CAP_EDGE",EDGE,{"disambiguationData":[OSD([subQ0]),TDD([makeQuery(id+"F0.imprint","IMPRINT",EDGE,{"disambiguationData":[TD([[makeQuery(id+"F0.imprint","INTERSECT",VERTEX,{"derivedFrom":[sQuery(id+"F0.wireOp",EDGE,"E1.bottom"),subQ0]}),-1.0]])],"derivedFrom":subQ0})])],"isStart":false});}
            var Q24;
            Q24=makeQuery(id+"F1.opExtrude","CAP_EDGE",EDGE,{"disambiguationData":[OSD([sQuery(id+"F0.wireOp",EDGE,"E41.top")])],"isStart":false});
            var Q25;
            Q25=makeQuery(id+"F1.opExtrude","CAP_EDGE",EDGE,{"disambiguationData":[OSD([sQuery(id+"F0.wireOp",EDGE,"E42.bottom")])],"isStart":false});
            var Q26;
            Q26=makeQuery(id+"F1.opExtrude","CAP_EDGE",EDGE,{"disambiguationData":[OSD([sQuery(id+"F0.wireOp",EDGE,"E42.top")])],"isStart":false});
            var Q27;
            {var subQ0=sQuery(id+"F0.wireOp",EDGE,"E1.right");Q27=makeQuery(id+"F1.opExtrude","CAP_EDGE",EDGE,{"disambiguationData":[OSD([subQ0]),TDD([makeQuery(id+"F0.imprint","IMPRINT",EDGE,{"disambiguationData":[TD([[makeQuery(id+"F0.imprint","INTERSECT",VERTEX,{"derivedFrom":[sQuery(id+"F0.wireOp",EDGE,"E1.top"),subQ0]}),1.0]])],"derivedFrom":subQ0})])],"isStart":false});}
            fillet(context, id + "F6", {"entities" : qUnion([Q0, Q1, Q2, Q3, Q4, Q5, Q6, Q7, Q8, Q9, Q10, Q11, Q12, Q13, Q14, Q15, Q16, Q17, Q18, Q19, Q20, Q21, Q22, Q23, Q24, Q25, Q26, Q27]), "radius" : 0.5 * mm, "tangentPropagation" : true, "allowEdgeOverflow" : false});
        }
        {
            var Q0;
            Q0=makeQuery(id+"F1.opExtrude","CAP_EDGE",EDGE,{"disambiguationData":[OSD([sQuery(id+"F0.wireOp",EDGE,"E2.bottom"),sQuery(id+"F0.wireOp",EDGE,"E37.top")])],"isStart":false});
            var Q1;
            Q1=makeQuery(id+"F1.opExtrude","CAP_EDGE",EDGE,{"disambiguationData":[OSD([sQuery(id+"F0.wireOp",EDGE,"E11.right")])],"isStart":false});
            var Q2;
            Q2=makeQuery(id+"F1.opExtrude","CAP_EDGE",EDGE,{"disambiguationData":[OSD([sQuery(id+"F0.wireOp",EDGE,"E11.left")])],"isStart":false});
            var Q3;
            {var subQ0=sQuery(id+"F0.wireOp",EDGE,"E2.bottom");Q3=makeQuery(id+"F1.opExtrude","CAP_EDGE",EDGE,{"disambiguationData":[OSD([subQ0]),TDD([makeQuery(id+"F0.imprint","IMPRINT",EDGE,{"disambiguationData":[TD([[makeQuery(id+"F0.imprint","INTERSECT",VERTEX,{"derivedFrom":[subQ0,sQuery(id+"F0.wireOp",EDGE,"E2.left")]}),-1.0]])],"derivedFrom":subQ0})])],"isStart":false});}
            var Q4;
            Q4=makeQuery(id+"F1.opExtrude","CAP_EDGE",EDGE,{"disambiguationData":[OSD([sQuery(id+"F0.wireOp",EDGE,"E50.bottom")])],"isStart":false});
            var Q5;
            {var subQ0=sQuery(id+"F0.wireOp",EDGE,"E2.left");Q5=makeQuery(id+"F1.opExtrude","CAP_EDGE",EDGE,{"disambiguationData":[OSD([subQ0]),TDD([makeQuery(id+"F0.imprint","IMPRINT",EDGE,{"disambiguationData":[TD([[makeQuery(id+"F0.imprint","INTERSECT",VERTEX,{"derivedFrom":[sQuery(id+"F0.wireOp",EDGE,"E2.bottom"),subQ0]}),-1.0]])],"derivedFrom":subQ0})])],"isStart":false});}
            var Q6;
            Q6=makeQuery(id+"F1.opExtrude","CAP_EDGE",EDGE,{"disambiguationData":[OSD([sQuery(id+"F0.wireOp",EDGE,"E50.top")])],"isStart":false});
            var Q7;
            Q7=makeQuery(id+"F1.opExtrude","CAP_EDGE",EDGE,{"disambiguationData":[OSD([sQuery(id+"F0.wireOp",EDGE,"E2.left"),sQuery(id+"F0.wireOp",EDGE,"E20.left")])],"isStart":false});
            var Q8;
            Q8=makeQuery(id+"F1.opExtrude","CAP_EDGE",EDGE,{"disambiguationData":[OSD([sQuery(id+"F0.wireOp",EDGE,"E45.bottom")])],"isStart":false});
            var Q9;
            Q9=makeQuery(id+"F1.opExtrude","CAP_EDGE",EDGE,{"disambiguationData":[OSD([sQuery(id+"F0.wireOp",EDGE,"E45.top")])],"isStart":false});
            var Q10;
            {var subQ0=sQuery(id+"F0.wireOp",EDGE,"E2.left");Q10=makeQuery(id+"F1.opExtrude","CAP_EDGE",EDGE,{"disambiguationData":[OSD([subQ0]),TDD([makeQuery(id+"F0.imprint","IMPRINT",EDGE,{"disambiguationData":[TD([[makeQuery(id+"F0.imprint","INTERSECT",VERTEX,{"derivedFrom":[sQuery(id+"F0.wireOp",EDGE,"E2.top"),subQ0]}),1.0]])],"derivedFrom":subQ0})])],"isStart":false});}
            var Q11;
            {var subQ0=sQuery(id+"F0.wireOp",EDGE,"E2.top");Q11=makeQuery(id+"F1.opExtrude","CAP_EDGE",EDGE,{"disambiguationData":[OSD([subQ0]),TDD([makeQuery(id+"F0.imprint","IMPRINT",EDGE,{"disambiguationData":[TD([[makeQuery(id+"F0.imprint","INTERSECT",VERTEX,{"derivedFrom":[subQ0,sQuery(id+"F0.wireOp",EDGE,"E2.left")]}),-1.0]])],"derivedFrom":subQ0})])],"isStart":false});}
            var Q12;
            Q12=makeQuery(id+"F1.opExtrude","CAP_EDGE",EDGE,{"disambiguationData":[OSD([sQuery(id+"F0.wireOp",EDGE,"E13.left")])],"isStart":false});
            var Q13;
            Q13=makeQuery(id+"F1.opExtrude","CAP_EDGE",EDGE,{"disambiguationData":[OSD([sQuery(id+"F0.wireOp",EDGE,"E13.right")])],"isStart":false});
            var Q14;
            Q14=makeQuery(id+"F1.opExtrude","CAP_EDGE",EDGE,{"disambiguationData":[OSD([sQuery(id+"F0.wireOp",EDGE,"E2.top"),sQuery(id+"F0.wireOp",EDGE,"E38.bottom")])],"isStart":false});
            var Q15;
            Q15=makeQuery(id+"F1.opExtrude","CAP_EDGE",EDGE,{"disambiguationData":[OSD([sQuery(id+"F0.wireOp",EDGE,"E14.left")])],"isStart":false});
            var Q16;
            Q16=makeQuery(id+"F1.opExtrude","CAP_EDGE",EDGE,{"disambiguationData":[OSD([sQuery(id+"F0.wireOp",EDGE,"E14.right")])],"isStart":false});
            var Q17;
            {var subQ0=sQuery(id+"F0.wireOp",EDGE,"E2.top");Q17=makeQuery(id+"F1.opExtrude","CAP_EDGE",EDGE,{"disambiguationData":[OSD([subQ0]),TDD([makeQuery(id+"F0.imprint","IMPRINT",EDGE,{"disambiguationData":[TD([[makeQuery(id+"F0.imprint","INTERSECT",VERTEX,{"derivedFrom":[subQ0,sQuery(id+"F0.wireOp",EDGE,"E2.right")]}),1.0]])],"derivedFrom":subQ0})])],"isStart":false});}
            var Q18;
            {var subQ0=sQuery(id+"F0.wireOp",EDGE,"E2.right");Q18=makeQuery(id+"F1.opExtrude","CAP_EDGE",EDGE,{"disambiguationData":[OSD([subQ0]),TDD([makeQuery(id+"F0.imprint","IMPRINT",EDGE,{"disambiguationData":[TD([[makeQuery(id+"F0.imprint","INTERSECT",VERTEX,{"derivedFrom":[sQuery(id+"F0.wireOp",EDGE,"E2.top"),subQ0]}),1.0]])],"derivedFrom":subQ0})])],"isStart":false});}
            var Q19;
            Q19=makeQuery(id+"F1.opExtrude","CAP_EDGE",EDGE,{"disambiguationData":[OSD([sQuery(id+"F0.wireOp",EDGE,"E49.top")])],"isStart":false});
            var Q20;
            Q20=makeQuery(id+"F1.opExtrude","CAP_EDGE",EDGE,{"disambiguationData":[OSD([sQuery(id+"F0.wireOp",EDGE,"E49.bottom")])],"isStart":false});
            var Q21;
            Q21=makeQuery(id+"F1.opExtrude","CAP_EDGE",EDGE,{"disambiguationData":[OSD([sQuery(id+"F0.wireOp",EDGE,"E2.right"),sQuery(id+"F0.wireOp",EDGE,"E19.left")])],"isStart":false});
            var Q22;
            Q22=makeQuery(id+"F1.opExtrude","CAP_EDGE",EDGE,{"disambiguationData":[OSD([sQuery(id+"F0.wireOp",EDGE,"E48.top")])],"isStart":false});
            var Q23;
            Q23=makeQuery(id+"F1.opExtrude","CAP_EDGE",EDGE,{"disambiguationData":[OSD([sQuery(id+"F0.wireOp",EDGE,"E48.bottom")])],"isStart":false});
            var Q24;
            {var subQ0=sQuery(id+"F0.wireOp",EDGE,"E2.right");Q24=makeQuery(id+"F1.opExtrude","CAP_EDGE",EDGE,{"disambiguationData":[OSD([subQ0]),TDD([makeQuery(id+"F0.imprint","IMPRINT",EDGE,{"disambiguationData":[TD([[makeQuery(id+"F0.imprint","INTERSECT",VERTEX,{"derivedFrom":[sQuery(id+"F0.wireOp",EDGE,"E2.bottom"),subQ0]}),-1.0]])],"derivedFrom":subQ0})])],"isStart":false});}
            var Q25;
            {var subQ0=sQuery(id+"F0.wireOp",EDGE,"E2.bottom");Q25=makeQuery(id+"F1.opExtrude","CAP_EDGE",EDGE,{"disambiguationData":[OSD([subQ0]),TDD([makeQuery(id+"F0.imprint","IMPRINT",EDGE,{"disambiguationData":[TD([[makeQuery(id+"F0.imprint","INTERSECT",VERTEX,{"derivedFrom":[subQ0,sQuery(id+"F0.wireOp",EDGE,"E2.right")]}),1.0]])],"derivedFrom":subQ0})])],"isStart":false});}
            var Q26;
            Q26=makeQuery(id+"F1.opExtrude","CAP_EDGE",EDGE,{"disambiguationData":[OSD([sQuery(id+"F0.wireOp",EDGE,"E12.right")])],"isStart":false});
            var Q27;
            Q27=makeQuery(id+"F1.opExtrude","CAP_EDGE",EDGE,{"disambiguationData":[OSD([sQuery(id+"F0.wireOp",EDGE,"E12.left")])],"isStart":false});
            fillet(context, id + "F7", {"entities" : qUnion([Q0, Q1, Q2, Q3, Q4, Q5, Q6, Q7, Q8, Q9, Q10, Q11, Q12, Q13, Q14, Q15, Q16, Q17, Q18, Q19, Q20, Q21, Q22, Q23, Q24, Q25, Q26, Q27]), "radius" : 0.5 * mm, "tangentPropagation" : true, "allowEdgeOverflow" : false});
        }
    });
